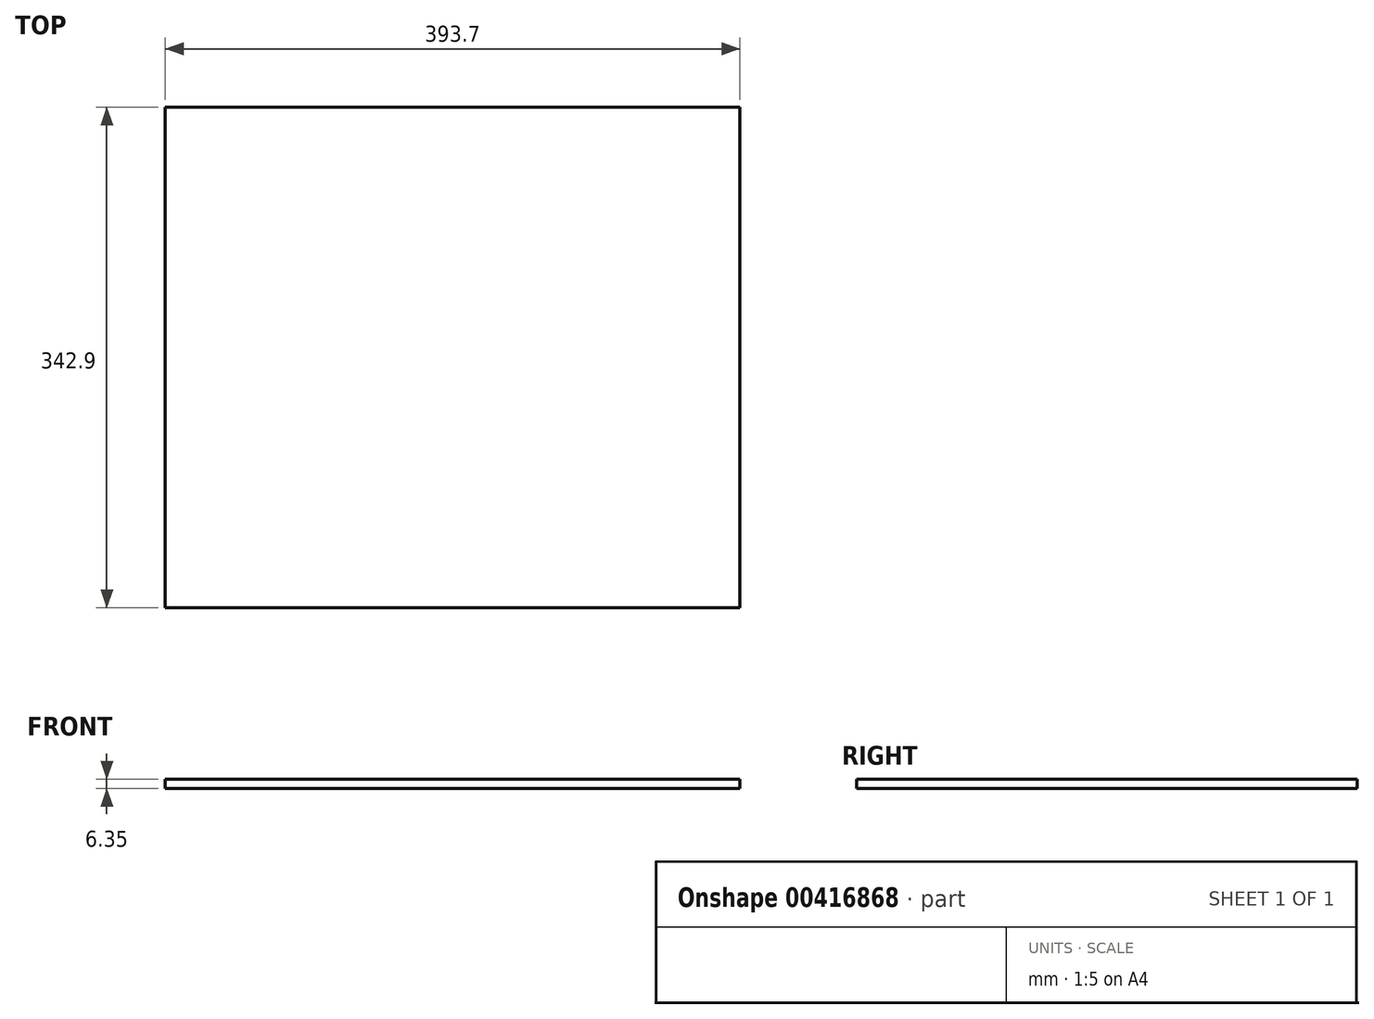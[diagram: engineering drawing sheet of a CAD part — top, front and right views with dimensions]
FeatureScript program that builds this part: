
annotation { "Feature Type Name" : "Feature", "Feature Type Description" : "" }
export const myFeature = defineFeature(function(context is Context, id is Id, definition is map)
    precondition{}
    {
        {
            var Q0;
            Q0=qCreatedBy(makeId("Top.planeOp"),FACE);
            var sketch = newSketch(context, id + "F0", { "sketchPlane" : qUnion([Q0])});
            skLineSegment(sketch, "E0.bottom", {"start": v(-196.85, 171.45) * mm, "end": v(196.85, 171.45) * mm});
            skLineSegment(sketch, "E0.top", {"start": v(-196.85, -171.45) * mm, "end": v(196.85, -171.45) * mm});
            skLineSegment(sketch, "E0.left", {"start": v(-196.85, 171.45) * mm, "end": v(-196.85, -171.45) * mm});
            skLineSegment(sketch, "E0.right", {"start": v(196.85, 171.45) * mm, "end": v(196.85, -171.45) * mm});
            skPoint(sketch, "E0.middle", {"position": v(0, 0) * mm});
            skSolve(sketch);
        }
        {
            var Q0;
            Q0 = qSketchRegion(id + "F0", true);
            extrude(context, id + "F1", {"entities" : qUnion([Q0]), "depth" : 6.35 * mm});
        }
    });
